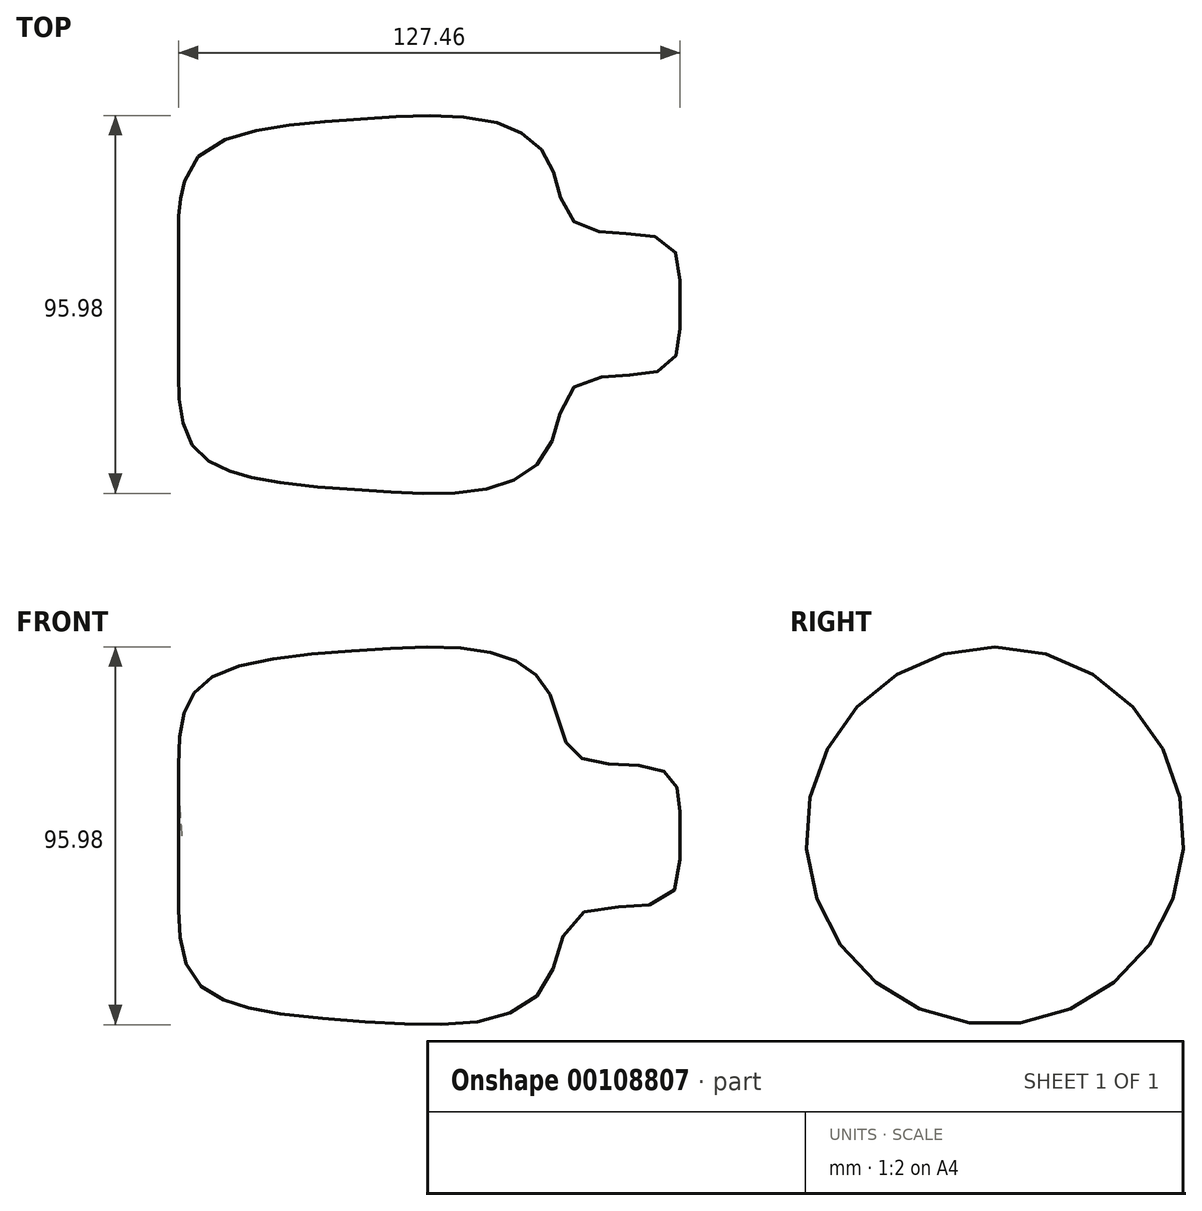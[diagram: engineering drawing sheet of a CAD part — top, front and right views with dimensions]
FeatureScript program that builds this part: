
annotation { "Feature Type Name" : "Feature", "Feature Type Description" : "" }
export const myFeature = defineFeature(function(context is Context, id is Id, definition is map)
    precondition{}
    {
        {
            var Q0;
            Q0=qCreatedBy(makeId("Front.planeOp"),FACE);
            var sketch = newSketch(context, id + "F0", { "sketchPlane" : qUnion([Q0])});
            skFitSpline(sketch, "E0", {"points": [v(-57.33, 0) * mm, v(-57.71, 27.02) * mm, v(-50, 40.15) * mm, v(-12.93, 47.1) * mm, v(22.2, 46.32) * mm, v(36.1, 35.9) * mm, v(43.43, 20.07) * mm, v(65.43, 16.21) * mm, v(68.9, 0) * mm], "startDerivative": vector(-16.84, 215.23) * mm, "endDerivative": vector(-12.44, -191.56) * mm});
            skLineSegment(sketch, "E1", {"start": v(-57.33, 0) * mm, "end": v(68.9, 0) * mm});
            skSolve(sketch);
        }
        {
            var Q0;
            Q0=makeQuery(id+"F0.imprint","IMPRINT",FACE,{"disambiguationData":[TD([[makeQuery(id+"F0.imprint","IMPRINT",EDGE,{"derivedFrom":sQuery(id+"F0.wireOp",EDGE,"E0")}),-1.0]])]});
            var Q1;
            Q1=sQuery(id+"F0.wireOp",EDGE,"E1");
            revolve(context, id + "F1", {"entities" : qUnion([Q0]), "axis" : qUnion([Q1]), "revolveType" : RevolveType.FULL});
        }
    });
